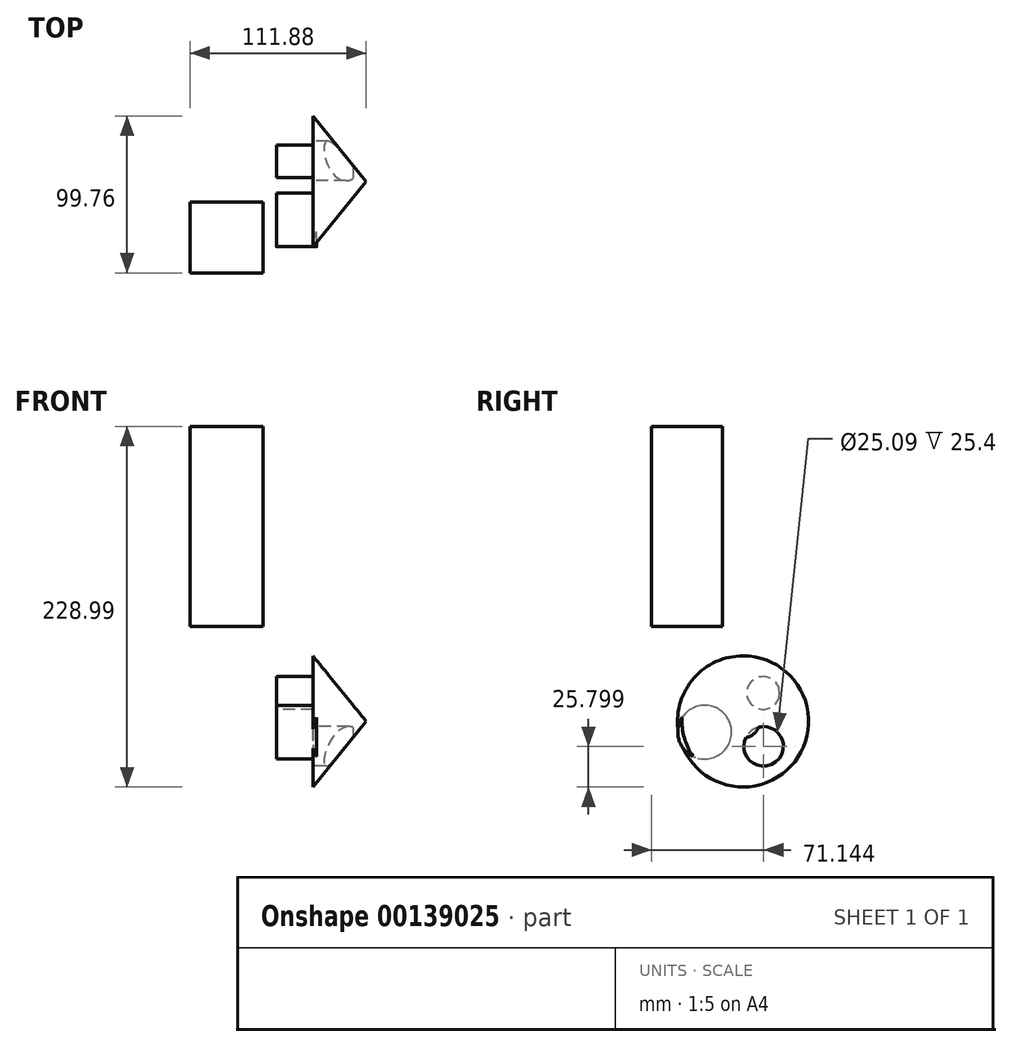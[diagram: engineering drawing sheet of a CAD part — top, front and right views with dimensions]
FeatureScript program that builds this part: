
annotation { "Feature Type Name" : "Feature", "Feature Type Description" : "" }
export const myFeature = defineFeature(function(context is Context, id is Id, definition is map)
    precondition{}
    {
        {
            var Q0;
            Q0=qCreatedBy(makeId("Top.planeOp"),FACE);
            var sketch = newSketch(context, id + "F0", { "sketchPlane" : qUnion([Q0])});
            skLineSegment(sketch, "E0.bottom", {"start": v(-54.9, -13) * mm, "end": v(-8.64, -13) * mm});
            skLineSegment(sketch, "E0.top", {"start": v(-54.9, -58.12) * mm, "end": v(-8.64, -58.12) * mm});
            skLineSegment(sketch, "E0.left", {"start": v(-54.9, -13) * mm, "end": v(-54.9, -58.12) * mm});
            skLineSegment(sketch, "E0.right", {"start": v(-8.64, -13) * mm, "end": v(-8.64, -58.12) * mm});
            skSolve(sketch);
        }
        {
            var Q0;
            Q0=makeQuery(id+"F0.imprint","IMPRINT",FACE,{"disambiguationData":[TD([[makeQuery(id+"F0.imprint","IMPRINT",EDGE,{"derivedFrom":sQuery(id+"F0.wireOp",EDGE,"E0.bottom")}),-1.0]])]});
            extrude(context, id + "F1", {"entities" : qUnion([Q0]), "depth" : 127 * mm});
        }
        {
            var Q0;
            Q0=qCreatedBy(makeId("Front.planeOp"),FACE);
            var sketch = newSketch(context, id + "F2", { "sketchPlane" : qUnion([Q0])});
            skLineSegment(sketch, "E1", {"start": v(23.08, -18.72) * mm, "end": v(23.08, -60.36) * mm});
            skLineSegment(sketch, "E2", {"start": v(23.08, -60.36) * mm, "end": v(56.97, -60.36) * mm});
            skLineSegment(sketch, "E3", {"start": v(56.97, -60.36) * mm, "end": v(23.08, -18.72) * mm});
            skSolve(sketch);
        }
        {
            var Q0;
            Q0=makeQuery(id+"F2.imprint","IMPRINT",FACE,{"disambiguationData":[TD([[makeQuery(id+"F2.imprint","IMPRINT",EDGE,{"derivedFrom":sQuery(id+"F2.wireOp",EDGE,"E1")}),1.0]])]});
            var Q1;
            Q1=sQuery(id+"F2.wireOp",EDGE,"E2");
            revolve(context, id + "F3", {"entities" : qUnion([Q0]), "axis" : qUnion([Q1]), "revolveType" : RevolveType.FULL});
        }
        {
            var Q0;
            Q0=qCreatedBy(makeId("Right.planeOp"),FACE);
            var sketch = newSketch(context, id + "F4", { "sketchPlane" : qUnion([Q0])});
            skCircle(sketch, "E4", {"center": v(12.75, -42.28) * mm, "radius": 10.4 * mm});
            skCircle(sketch, "E5", {"center": v(-24.37, -67.13) * mm, "radius": 17.08 * mm});
            skSolve(sketch);
        }
        {
            var Q0;
            Q0 = qSketchRegion(id + "F4", true);
            extrude(context, id + "F5", {"entities" : qUnion([Q0]), "operationType" : NewBodyOperationType.ADD, "depth" : 25.4 * mm});
        }
        {
            var Q0;
            Q0=makeQuery(id+"F3.opRevolve","SWEPT_FACE",FACE,{"disambiguationData":[OSD([sQuery(id+"F2.wireOp",EDGE,"E1")])]});
            var sketch = newSketch(context, id + "F6", { "sketchPlane" : qUnion([Q0])});
            skCircle(sketch, "E6", {"center": v(-13.02, -76.2) * mm, "radius": 12.55 * mm});
            skSolve(sketch);
        }
        {
            var Q0;
            Q0 = qSketchRegion(id + "F6", true);
            extrude(context, id + "F7", {"entities" : qUnion([Q0]), "operationType" : NewBodyOperationType.REMOVE, "oppositeDirection" : true, "depth" : 25.4 * mm});
        }
    });
